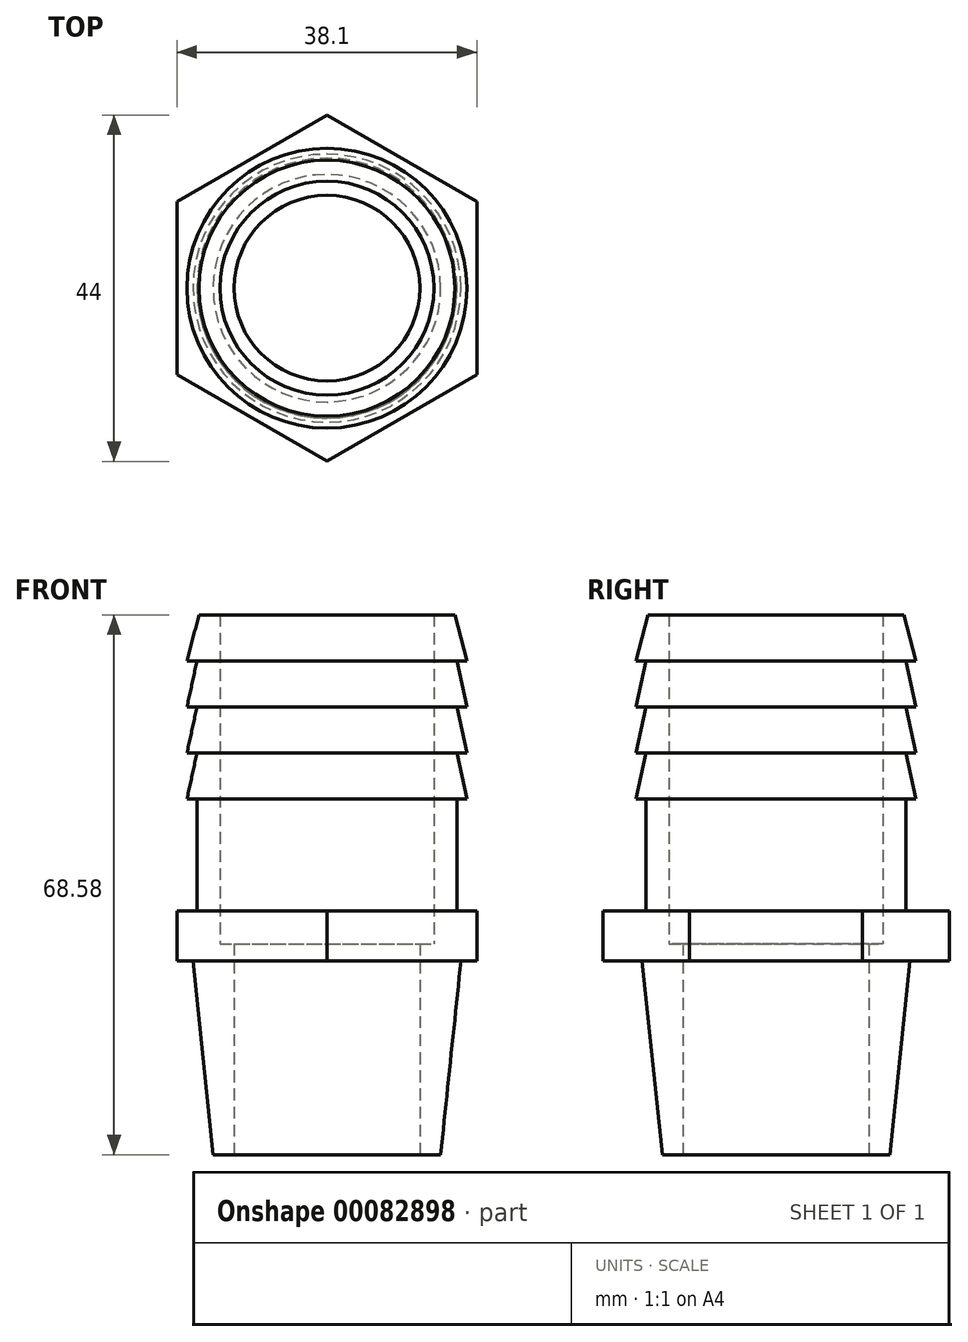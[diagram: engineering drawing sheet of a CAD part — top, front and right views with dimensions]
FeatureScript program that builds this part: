
annotation { "Feature Type Name" : "Feature", "Feature Type Description" : "" }
export const myFeature = defineFeature(function(context is Context, id is Id, definition is map)
    precondition{}
    {
        {
            var Q0;
            Q0=qCreatedBy(makeId("Front.planeOp"),FACE);
            var sketch = newSketch(context, id + "F0", { "sketchPlane" : qUnion([Q0])});
            skLineSegment(sketch, "E0.top", {"start": v(-13.59, 68.58) * mm, "end": v(-16.26, 68.58) * mm});
            skLineSegment(sketch, "E0.left", {"start": v(-13.59, 26.8) * mm, "end": v(-13.59, 68.58) * mm});
            skLineSegment(sketch, "E0.right", {"start": v(-16.5, 0) * mm, "end": v(-16.51, 45.21) * mm});
            skLineSegment(sketch, "E1", {"start": v(0, 0) * mm, "end": v(0, 68.58) * mm, "construction": true});
            skLineSegment(sketch, "E2", {"start": v(-13.59, 26.8) * mm, "end": v(-11.8, 26.8) * mm});
            skLineSegment(sketch, "E3", {"start": v(-11.8, 26.8) * mm, "end": v(-11.8, 0) * mm});
            skLineSegment(sketch, "E4", {"start": v(-16.5, 0) * mm, "end": v(-11.8, 0) * mm});
            skLineSegment(sketch, "E5", {"start": v(-16.26, 68.58) * mm, "end": v(-17.78, 62.74) * mm});
            skLineSegment(sketch, "E6", {"start": v(-17.78, 62.74) * mm, "end": v(-16.51, 62.74) * mm});
            skLineSegment(sketch, "E7", {"start": v(-16.51, 62.74) * mm, "end": v(-17.78, 56.9) * mm});
            skLineSegment(sketch, "E8", {"start": v(-17.78, 56.9) * mm, "end": v(-16.51, 56.9) * mm});
            skLineSegment(sketch, "E9", {"start": v(-16.51, 56.9) * mm, "end": v(-17.78, 51.05) * mm});
            skLineSegment(sketch, "E10", {"start": v(-17.78, 51.05) * mm, "end": v(-16.51, 51.05) * mm});
            skLineSegment(sketch, "E11", {"start": v(-16.51, 51.05) * mm, "end": v(-17.78, 45.21) * mm});
            skLineSegment(sketch, "E12", {"start": v(-17.78, 45.21) * mm, "end": v(-16.51, 45.21) * mm});
            skSolve(sketch);
        }
        {
            var Q0;
            Q0=makeQuery(id+"F0.imprint","IMPRINT",FACE,{"disambiguationData":[TD([[makeQuery(id+"F0.imprint","IMPRINT",EDGE,{"derivedFrom":sQuery(id+"F0.wireOp",EDGE,"E0.top")}),1.0]])]});
            var Q1;
            Q1=sQuery(id+"F0.wireOp",EDGE,"E1");
            revolve(context, id + "F1", {"entities" : qUnion([Q0]), "axis" : qUnion([Q1]), "revolveType" : RevolveType.FULL});
        }
        {
            var Q0;
            Q0=makeQuery(id+"F1.opRevolve","SWEPT_FACE",FACE,{"disambiguationData":[OSD([sQuery(id+"F0.wireOp",EDGE,"E0.top")])]});
            cPlane(context, id + "F2", {"entities" : qUnion([Q0]), "cplaneType" : CPlaneType.OFFSET, "offset" : 37.6 * mm, "oppositeDirection" : true, "width" : 152.4 * mm, "height" : 152.4 * mm});
        }
        {
            var Q0;
            Q0=qCreatedBy(id+"F2.planeOp",FACE);
            var sketch = newSketch(context, id + "F3", { "sketchPlane" : qUnion([Q0])});
            skCircle(sketch, "E13", {"center": v(0, 0) * mm, "radius": 16.51 * mm});
            skCircle(sketch, "E14.cCircle", {"center": v(0, 0) * mm, "radius": 19.05 * mm, "construction": true});
            skLineSegment(sketch, "E14.0", {"start": v(0, 22) * mm, "end": v(19.05, 11) * mm});
            skLineSegment(sketch, "E14.1", {"start": v(19.05, 11) * mm, "end": v(19.05, -11) * mm});
            skLineSegment(sketch, "E14.2", {"start": v(19.05, -11) * mm, "end": v(0, -22) * mm});
            skLineSegment(sketch, "E14.3", {"start": v(0, -22) * mm, "end": v(-19.05, -11) * mm});
            skLineSegment(sketch, "E14.4", {"start": v(-19.05, -11) * mm, "end": v(-19.05, 11) * mm});
            skLineSegment(sketch, "E14.5", {"start": v(-19.05, 11) * mm, "end": v(0, 22) * mm});
            skPoint(sketch, "E14.0.midPoint", {"position": v(9.53, 16.5) * mm});
            skSolve(sketch);
        }
        {
            var Q0;
            Q0 = qSketchRegion(id + "F3", true);
            extrude(context, id + "F4", {"entities" : qUnion([Q0]), "operationType" : NewBodyOperationType.ADD, "oppositeDirection" : true, "depth" : 6.35 * mm});
        }
        {
            var Q0;
            Q0=qCreatedBy(makeId("Front.planeOp"),FACE);
            var sketch = newSketch(context, id + "F5", { "sketchPlane" : qUnion([Q0])});
            skLineSegment(sketch, "E15", {"start": v(-17.02, 24.64) * mm, "end": v(-14.45, 0) * mm, "construction": true});
            skLineSegment(sketch, "E16", {"start": v(0, 0) * mm, "end": v(0, 24.64) * mm, "construction": true});
            skSolve(sketch);
        }
        {
            var Q0;
            Q0=qCreatedBy(makeId("Front.planeOp"),FACE);
            var sketch = newSketch(context, id + "F6", { "sketchPlane" : qUnion([Q0])});
            skLineSegment(sketch, "E17", {"start": v(-17.02, 24.64) * mm, "end": v(-16.51, 19.76) * mm});
            skLineSegment(sketch, "E18", {"start": v(-16.51, 19.76) * mm, "end": v(-16.51, 24.64) * mm});
            skLineSegment(sketch, "E19", {"start": v(-16.51, 24.64) * mm, "end": v(-17.02, 24.64) * mm});
            skLineSegment(sketch, "E20", {"start": v(-16.51, 0) * mm, "end": v(-16.51, 45.21) * mm, "construction": true});
            skLineSegment(sketch, "E21", {"start": v(16.51, 45.21) * mm, "end": v(16.51, 0) * mm});
            skLineSegment(sketch, "E22", {"start": v(0, 0) * mm, "end": v(0, 24.64) * mm, "construction": true});
            skSolve(sketch);
        }
        {
            var Q0;
            Q0 = qSketchRegion(id + "F6", true);
            var Q1;
            Q1 = qConstructionFilter(qBodyType(qCreatedBy(id + "F6" ,EDGE), BodyType.WIRE), ConstructionObject.NO);
            var Q2;
            Q2=sQuery(id+"F6.wireOp",EDGE,"E22");
            revolve(context, id + "F7", {"operationType" : NewBodyOperationType.ADD, "entities" : qUnion([Q0]), "surfaceEntities" : qUnion([Q1]), "axis" : qUnion([Q2]), "revolveType" : RevolveType.FULL});
        }
        {
            var Q0;
            Q0=qCreatedBy(makeId("Front.planeOp"),FACE);
            var sketch = newSketch(context, id + "F8", { "sketchPlane" : qUnion([Q0])});
            skLineSegment(sketch, "E23", {"start": v(-16.51, 19.76) * mm, "end": v(-14.45, 0) * mm});
            skLineSegment(sketch, "E24", {"start": v(-14.45, 0) * mm, "end": v(-16.51, 0) * mm});
            skLineSegment(sketch, "E25", {"start": v(-16.51, 0) * mm, "end": v(-16.51, 19.76) * mm});
            skLineSegment(sketch, "E26", {"start": v(-16.51, 0) * mm, "end": v(-16.51, 19.76) * mm, "construction": true});
            skSolve(sketch);
        }
        {
            var Q0;
            Q0 = qSketchRegion(id + "F8", true);
            var Q1;
            Q1=sQuery(id+"F5.wireOp",EDGE,"E16");
            revolve(context, id + "F9", {"operationType" : NewBodyOperationType.REMOVE, "entities" : qUnion([Q0]), "axis" : qUnion([Q1]), "revolveType" : RevolveType.FULL, "oppositeDirection" : true});
        }
    });
